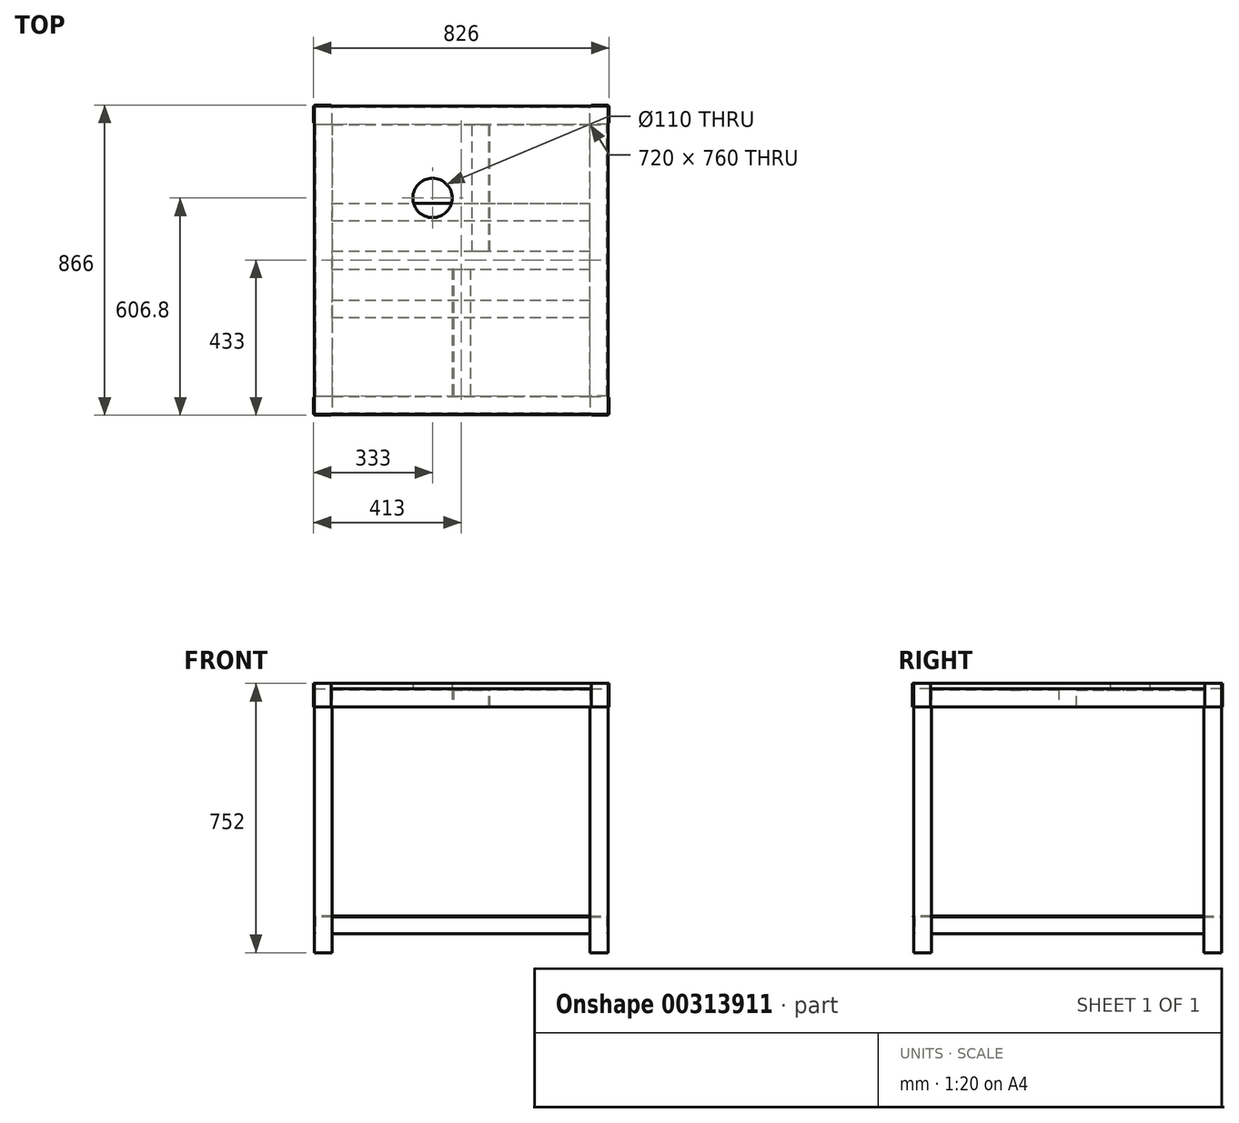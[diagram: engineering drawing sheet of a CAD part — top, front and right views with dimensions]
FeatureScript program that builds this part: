
annotation { "Feature Type Name" : "Feature", "Feature Type Description" : "" }
export const myFeature = defineFeature(function(context is Context, id is Id, definition is map)
    precondition{}
    {
        {
            var Q0;
            Q0=qCreatedBy(makeId("Top.planeOp"),FACE);
            var sketch = newSketch(context, id + "F0", { "sketchPlane" : qUnion([Q0])});
            skLineSegment(sketch, "E0", {"start": v(-475, -20) * mm, "end": v(-475, 410) * mm});
            skLineSegment(sketch, "E1", {"start": v(-475, -20) * mm, "end": v(-475, -450) * mm});
            skLineSegment(sketch, "E2", {"start": v(345, -20) * mm, "end": v(345, -450) * mm});
            skLineSegment(sketch, "E3", {"start": v(345, -20) * mm, "end": v(345, 410) * mm});
            skLineSegment(sketch, "E4", {"start": v(-425, -20) * mm, "end": v(-425, 360) * mm});
            skLineSegment(sketch, "E5", {"start": v(-425, -20) * mm, "end": v(-425, -400) * mm});
            skLineSegment(sketch, "E6", {"start": v(295, -20) * mm, "end": v(295, -400) * mm});
            skLineSegment(sketch, "E7", {"start": v(295, -20) * mm, "end": v(295, 360) * mm});
            skLineSegment(sketch, "E8", {"start": v(-425, 360) * mm, "end": v(295, 360) * mm});
            skLineSegment(sketch, "E9", {"start": v(-475, -450) * mm, "end": v(345, -450) * mm});
            skLineSegment(sketch, "E10", {"start": v(-425, -400) * mm, "end": v(295, -400) * mm});
            skLineSegment(sketch, "E11", {"start": v(-475, 410) * mm, "end": v(345, 410) * mm});
            skSolve(sketch);
        }
        {
            var Q0;
            Q0=makeQuery(id+"F0.imprint","IMPRINT",FACE,{"disambiguationData":[TD([[makeQuery(id+"F0.imprint","IMPRINT",EDGE,{"derivedFrom":sQuery(id+"F0.wireOp",EDGE,"E0")}),-1.0]])]});
            extrude(context, id + "F1", {"entities" : qUnion([Q0]), "depth" : 50 * mm});
        }
        {
            var Q0;
            Q0=makeQuery(id+"F1.opExtrude","SWEPT_BODY",BODY,{"disambiguationData":[OSD([sQuery(id+"F0.wireOp",EDGE,"E0"),sQuery(id+"F0.wireOp",EDGE,"E1"),sQuery(id+"F0.wireOp",EDGE,"E2"),sQuery(id+"F0.wireOp",EDGE,"E3"),sQuery(id+"F0.wireOp",EDGE,"E4"),sQuery(id+"F0.wireOp",EDGE,"E5"),sQuery(id+"F0.wireOp",EDGE,"E6"),sQuery(id+"F0.wireOp",EDGE,"E7"),sQuery(id+"F0.wireOp",EDGE,"E8"),sQuery(id+"F0.wireOp",EDGE,"E9"),sQuery(id+"F0.wireOp",EDGE,"E10"),sQuery(id+"F0.wireOp",EDGE,"E11")])]});
            transform(context, id + "F2", {"entities" : qUnion([Q0]), "transformType" : TransformType.TRANSLATION_3D, "dx" : 65 * mm, "dy" : 20 * mm, "dz" : 0 * mm, "makeCopy" : false});
        }
        {
            var Q0;
            Q0=makeQuery(id+"F1.opExtrude","SWEPT_BODY",BODY,{"disambiguationData":[OSD([sQuery(id+"F0.wireOp",EDGE,"E0"),sQuery(id+"F0.wireOp",EDGE,"E1"),sQuery(id+"F0.wireOp",EDGE,"E2"),sQuery(id+"F0.wireOp",EDGE,"E3"),sQuery(id+"F0.wireOp",EDGE,"E4"),sQuery(id+"F0.wireOp",EDGE,"E5"),sQuery(id+"F0.wireOp",EDGE,"E6"),sQuery(id+"F0.wireOp",EDGE,"E7"),sQuery(id+"F0.wireOp",EDGE,"E8"),sQuery(id+"F0.wireOp",EDGE,"E9"),sQuery(id+"F0.wireOp",EDGE,"E10"),sQuery(id+"F0.wireOp",EDGE,"E11")])]});
            transform(context, id + "F3", {"entities" : qUnion([Q0]), "transformType" : TransformType.TRANSLATION_3D, "dx" : 0 * mm, "dy" : 0 * mm, "dz" : -162 * mm, "makeCopy" : false});
        }
        {
            var Q0;
            Q0=qCreatedBy(makeId("Top.planeOp"),FACE);
            var sketch = newSketch(context, id + "F4", { "sketchPlane" : qUnion([Q0])});
            skLineSegment(sketch, "E12", {"start": v(-450, -20) * mm, "end": v(-450, 410) * mm});
            skLineSegment(sketch, "E13", {"start": v(370, -20) * mm, "end": v(370, -450) * mm});
            skLineSegment(sketch, "E14.bottom", {"start": v(-450, 410) * mm, "end": v(370, 410) * mm});
            skLineSegment(sketch, "E14.top", {"start": v(-450, -450) * mm, "end": v(370, -450) * mm});
            skLineSegment(sketch, "E14.left", {"start": v(-450, 410) * mm, "end": v(-450, -450) * mm});
            skLineSegment(sketch, "E14.right", {"start": v(370, 410) * mm, "end": v(370, -450) * mm});
            skSolve(sketch);
        }
        {
            var Q0;
            {var subQ0=sQuery(id+"F4.wireOp",EDGE,"E14.bottom");Q0=makeQuery(id+"F4.imprint","IMPRINT",FACE,{"disambiguationData":[TD([[makeQuery(id+"F4.imprint","IMPRINT",EDGE,{"derivedFrom":subQ0}),-1.0]])]});}
            extrude(context, id + "F5", {"entities" : qUnion([Q0]), "depth" : 15 * mm});
        }
        {
            var Q0;
            Q0=makeQuery(id+"F5.opExtrude","SWEPT_BODY",BODY,{"disambiguationData":[OSD([sQuery(id+"F4.wireOp",EDGE,"E14.bottom"),sQuery(id+"F4.wireOp",EDGE,"E14.top"),sQuery(id+"F4.wireOp",EDGE,"E14.left"),sQuery(id+"F4.wireOp",EDGE,"E14.right")])]});
            transform(context, id + "F6", {"entities" : qUnion([Q0]), "transformType" : TransformType.TRANSLATION_3D, "dx" : 0 * mm, "dy" : 0 * mm, "dz" : -112 * mm, "makeCopy" : false});
        }
        {
            var Q0;
            Q0=qCreatedBy(makeId("Top.planeOp"),FACE);
            var sketch = newSketch(context, id + "F7", { "sketchPlane" : qUnion([Q0])});
            skLineSegment(sketch, "E15", {"start": v(0, 0) * mm, "end": v(-410, 0) * mm});
            skLineSegment(sketch, "E16", {"start": v(0, 0) * mm, "end": v(410, 0) * mm});
            skLineSegment(sketch, "E17", {"start": v(-410, 0) * mm, "end": v(-410, 380) * mm});
            skLineSegment(sketch, "E18", {"start": v(410, 0) * mm, "end": v(410, 380) * mm});
            skLineSegment(sketch, "E19", {"start": v(-410, 0) * mm, "end": v(-410, -380) * mm});
            skLineSegment(sketch, "E20", {"start": v(410, 0) * mm, "end": v(410, -380) * mm});
            skLineSegment(sketch, "E21.bottom", {"start": v(-410, 380) * mm, "end": v(-360, 380) * mm});
            skLineSegment(sketch, "E21.top", {"start": v(-410, 430) * mm, "end": v(-360, 430) * mm});
            skLineSegment(sketch, "E21.left", {"start": v(-410, 380) * mm, "end": v(-410, 430) * mm});
            skLineSegment(sketch, "E21.right", {"start": v(-360, 380) * mm, "end": v(-360, 430) * mm});
            skLineSegment(sketch, "E22.bottom", {"start": v(-410, -380) * mm, "end": v(-360, -380) * mm});
            skLineSegment(sketch, "E22.top", {"start": v(-410, -430) * mm, "end": v(-360, -430) * mm});
            skLineSegment(sketch, "E22.left", {"start": v(-410, -380) * mm, "end": v(-410, -430) * mm});
            skLineSegment(sketch, "E22.right", {"start": v(-360, -380) * mm, "end": v(-360, -430) * mm});
            skLineSegment(sketch, "E23.bottom", {"start": v(410, -380) * mm, "end": v(360, -380) * mm});
            skLineSegment(sketch, "E23.top", {"start": v(410, -430) * mm, "end": v(360, -430) * mm});
            skLineSegment(sketch, "E23.left", {"start": v(410, -380) * mm, "end": v(410, -430) * mm});
            skLineSegment(sketch, "E23.right", {"start": v(360, -380) * mm, "end": v(360, -430) * mm});
            skLineSegment(sketch, "E24.bottom", {"start": v(410, 380) * mm, "end": v(360, 380) * mm});
            skLineSegment(sketch, "E24.top", {"start": v(410, 430) * mm, "end": v(360, 430) * mm});
            skLineSegment(sketch, "E24.left", {"start": v(410, 380) * mm, "end": v(410, 430) * mm});
            skLineSegment(sketch, "E24.right", {"start": v(360, 380) * mm, "end": v(360, 430) * mm});
            skLineSegment(sketch, "E25", {"start": v(-410, 0) * mm, "end": v(-410, -430) * mm});
            skLineSegment(sketch, "E26", {"start": v(-410, 0) * mm, "end": v(-410, 430) * mm});
            skSolve(sketch);
        }
        {
            var Q0;
            Q0=qSketchRegion(id+"F7",true);
            extrude(context, id + "F8", {"entities" : qUnion([Q0]), "depth" : 687 * mm});
        }
        {
            var Q0;
            Q0=makeQuery(id+"F8.opExtrude","SWEPT_BODY",BODY,{"disambiguationData":[OSD([sQuery(id+"F7.wireOp",EDGE,"E21.bottom"),sQuery(id+"F7.wireOp",EDGE,"E21.top"),sQuery(id+"F7.wireOp",EDGE,"E21.left"),sQuery(id+"F7.wireOp",EDGE,"E21.right")])]});
            var Q1;
            Q1=makeQuery(id+"F8.opExtrude","SWEPT_BODY",BODY,{"disambiguationData":[OSD([sQuery(id+"F7.wireOp",EDGE,"E22.bottom"),sQuery(id+"F7.wireOp",EDGE,"E22.top"),sQuery(id+"F7.wireOp",EDGE,"E22.left"),sQuery(id+"F7.wireOp",EDGE,"E22.right")])]});
            var Q2;
            Q2=makeQuery(id+"F8.opExtrude","SWEPT_BODY",BODY,{"disambiguationData":[OSD([sQuery(id+"F7.wireOp",EDGE,"E23.bottom"),sQuery(id+"F7.wireOp",EDGE,"E23.top"),sQuery(id+"F7.wireOp",EDGE,"E23.left"),sQuery(id+"F7.wireOp",EDGE,"E23.right")])]});
            var Q3;
            Q3=makeQuery(id+"F8.opExtrude","SWEPT_BODY",BODY,{"disambiguationData":[OSD([sQuery(id+"F7.wireOp",EDGE,"E24.bottom"),sQuery(id+"F7.wireOp",EDGE,"E24.top"),sQuery(id+"F7.wireOp",EDGE,"E24.left"),sQuery(id+"F7.wireOp",EDGE,"E24.right")])]});
            transform(context, id + "F9", {"entities" : qUnion([Q0, Q1, Q2, Q3]), "transformType" : TransformType.TRANSLATION_3D, "dx" : 0 * mm, "dy" : 0 * mm, "dz" : -849 * mm, "makeCopy" : false});
        }
        {
            var Q0;
            Q0=qCreatedBy(makeId("Top.planeOp"),FACE);
            var sketch = newSketch(context, id + "F10", { "sketchPlane" : qUnion([Q0])});
            skLineSegment(sketch, "E27", {"start": v(0, 0) * mm, "end": v(-410, 0) * mm});
            skLineSegment(sketch, "E28", {"start": v(0, 0) * mm, "end": v(410, 0) * mm});
            skLineSegment(sketch, "E29", {"start": v(-410, 0) * mm, "end": v(-410, -383) * mm});
            skLineSegment(sketch, "E30", {"start": v(410, 0) * mm, "end": v(410, -383) * mm});
            skLineSegment(sketch, "E31", {"start": v(-410, 0) * mm, "end": v(-410, 383) * mm});
            skLineSegment(sketch, "E32", {"start": v(410, 0) * mm, "end": v(410, 383) * mm});
            skLineSegment(sketch, "E33.bottom", {"start": v(-410, 383) * mm, "end": v(-413, 383) * mm});
            skLineSegment(sketch, "E33.top", {"start": v(-410, 433) * mm, "end": v(-413, 433) * mm});
            skLineSegment(sketch, "E33.left", {"start": v(-410, 383) * mm, "end": v(-410, 433) * mm});
            skLineSegment(sketch, "E33.right", {"start": v(-413, 383) * mm, "end": v(-413, 433) * mm});
            skLineSegment(sketch, "E34.bottom", {"start": v(-410, -383) * mm, "end": v(-413, -383) * mm});
            skLineSegment(sketch, "E34.top", {"start": v(-410, -433) * mm, "end": v(-413, -433) * mm});
            skLineSegment(sketch, "E34.left", {"start": v(-410, -383) * mm, "end": v(-410, -433) * mm});
            skLineSegment(sketch, "E34.right", {"start": v(-413, -383) * mm, "end": v(-413, -433) * mm});
            skLineSegment(sketch, "E35.bottom", {"start": v(410, -383) * mm, "end": v(413, -383) * mm});
            skLineSegment(sketch, "E35.top", {"start": v(410, -433) * mm, "end": v(413, -433) * mm});
            skLineSegment(sketch, "E35.left", {"start": v(410, -383) * mm, "end": v(410, -433) * mm});
            skLineSegment(sketch, "E35.right", {"start": v(413, -383) * mm, "end": v(413, -433) * mm});
            skLineSegment(sketch, "E36.bottom", {"start": v(410, 383) * mm, "end": v(413, 383) * mm});
            skLineSegment(sketch, "E36.top", {"start": v(410, 433) * mm, "end": v(413, 433) * mm});
            skLineSegment(sketch, "E36.left", {"start": v(410, 383) * mm, "end": v(410, 433) * mm});
            skLineSegment(sketch, "E36.right", {"start": v(413, 383) * mm, "end": v(413, 433) * mm});
            skLineSegment(sketch, "E37.bottom", {"start": v(-413, -433) * mm, "end": v(-363, -433) * mm});
            skLineSegment(sketch, "E37.top", {"start": v(-413, -430) * mm, "end": v(-363, -430) * mm});
            skLineSegment(sketch, "E37.left", {"start": v(-413, -433) * mm, "end": v(-413, -430) * mm});
            skLineSegment(sketch, "E37.right", {"start": v(-363, -433) * mm, "end": v(-363, -430) * mm});
            skLineSegment(sketch, "E38.bottom", {"start": v(413, -433) * mm, "end": v(363, -433) * mm});
            skLineSegment(sketch, "E38.top", {"start": v(413, -430) * mm, "end": v(363, -430) * mm});
            skLineSegment(sketch, "E38.left", {"start": v(413, -433) * mm, "end": v(413, -430) * mm});
            skLineSegment(sketch, "E38.right", {"start": v(363, -433) * mm, "end": v(363, -430) * mm});
            skLineSegment(sketch, "E39.bottom", {"start": v(-413, 433) * mm, "end": v(-363, 433) * mm});
            skLineSegment(sketch, "E39.top", {"start": v(-413, 430) * mm, "end": v(-363, 430) * mm});
            skLineSegment(sketch, "E39.left", {"start": v(-413, 433) * mm, "end": v(-413, 430) * mm});
            skLineSegment(sketch, "E39.right", {"start": v(-363, 433) * mm, "end": v(-363, 430) * mm});
            skLineSegment(sketch, "E40.bottom", {"start": v(413, 433) * mm, "end": v(363, 433) * mm});
            skLineSegment(sketch, "E40.top", {"start": v(413, 430) * mm, "end": v(363, 430) * mm});
            skLineSegment(sketch, "E40.left", {"start": v(413, 433) * mm, "end": v(413, 430) * mm});
            skLineSegment(sketch, "E40.right", {"start": v(363, 433) * mm, "end": v(363, 430) * mm});
            skSolve(sketch);
        }
        {
            var Q0;
            {var subQ0=sQuery(id+"F10.wireOp",EDGE,"E33.bottom");Q0=makeQuery(id+"F10.imprint","IMPRINT",FACE,{"disambiguationData":[TD([[makeQuery(id+"F10.imprint","IMPRINT",EDGE,{"derivedFrom":subQ0}),-1.0]])]});}
            var Q1;
            {var subQ5=sQuery(id+"F10.wireOp",EDGE,"E39.left");Q1=makeQuery(id+"F10.imprint","IMPRINT",FACE,{"disambiguationData":[TD([[makeQuery(id+"F10.imprint","IMPRINT",EDGE,{"derivedFrom":subQ5}),1.0]])]});}
            var Q2;
            {var subQ5=sQuery(id+"F10.wireOp",EDGE,"E39.right");Q2=makeQuery(id+"F10.imprint","IMPRINT",FACE,{"disambiguationData":[TD([[makeQuery(id+"F10.imprint","IMPRINT",EDGE,{"derivedFrom":subQ5}),-1.0]])]});}
            var Q3;
            {var subQ0=sQuery(id+"F10.wireOp",EDGE,"E34.bottom");Q3=makeQuery(id+"F10.imprint","IMPRINT",FACE,{"disambiguationData":[TD([[makeQuery(id+"F10.imprint","IMPRINT",EDGE,{"derivedFrom":subQ0}),1.0]])]});}
            var Q4;
            {var subQ5=sQuery(id+"F10.wireOp",EDGE,"E37.left");Q4=makeQuery(id+"F10.imprint","IMPRINT",FACE,{"disambiguationData":[TD([[makeQuery(id+"F10.imprint","IMPRINT",EDGE,{"derivedFrom":subQ5}),-1.0]])]});}
            var Q5;
            {var subQ5=sQuery(id+"F10.wireOp",EDGE,"E37.right");Q5=makeQuery(id+"F10.imprint","IMPRINT",FACE,{"disambiguationData":[TD([[makeQuery(id+"F10.imprint","IMPRINT",EDGE,{"derivedFrom":subQ5}),1.0]])]});}
            var Q6;
            {var subQ5=sQuery(id+"F10.wireOp",EDGE,"E38.right");Q6=makeQuery(id+"F10.imprint","IMPRINT",FACE,{"disambiguationData":[TD([[makeQuery(id+"F10.imprint","IMPRINT",EDGE,{"derivedFrom":subQ5}),-1.0]])]});}
            var Q7;
            {var subQ5=sQuery(id+"F10.wireOp",EDGE,"E38.left");Q7=makeQuery(id+"F10.imprint","IMPRINT",FACE,{"disambiguationData":[TD([[makeQuery(id+"F10.imprint","IMPRINT",EDGE,{"derivedFrom":subQ5}),1.0]])]});}
            var Q8;
            {var subQ0=sQuery(id+"F10.wireOp",EDGE,"E35.bottom");Q8=makeQuery(id+"F10.imprint","IMPRINT",FACE,{"disambiguationData":[TD([[makeQuery(id+"F10.imprint","IMPRINT",EDGE,{"derivedFrom":subQ0}),-1.0]])]});}
            var Q9;
            {var subQ0=sQuery(id+"F10.wireOp",EDGE,"E36.bottom");Q9=makeQuery(id+"F10.imprint","IMPRINT",FACE,{"disambiguationData":[TD([[makeQuery(id+"F10.imprint","IMPRINT",EDGE,{"derivedFrom":subQ0}),1.0]])]});}
            var Q10;
            {var subQ5=sQuery(id+"F10.wireOp",EDGE,"E40.left");Q10=makeQuery(id+"F10.imprint","IMPRINT",FACE,{"disambiguationData":[TD([[makeQuery(id+"F10.imprint","IMPRINT",EDGE,{"derivedFrom":subQ5}),-1.0]])]});}
            var Q11;
            {var subQ5=sQuery(id+"F10.wireOp",EDGE,"E40.right");Q11=makeQuery(id+"F10.imprint","IMPRINT",FACE,{"disambiguationData":[TD([[makeQuery(id+"F10.imprint","IMPRINT",EDGE,{"derivedFrom":subQ5}),1.0]])]});}
            extrude(context, id + "F11", {"entities" : qUnion([Q0, Q1, Q2, Q3, Q4, Q5, Q6, Q7, Q8, Q9, Q10, Q11]), "depth" : 65 * mm});
        }
        {
            var Q0;
            Q0=makeQuery(id+"F11.opExtrude","SWEPT_BODY",BODY,{"disambiguationData":[OSD([sQuery(id+"F10.wireOp",EDGE,"E33.bottom"),sQuery(id+"F10.wireOp",EDGE,"E33.left"),sQuery(id+"F10.wireOp",EDGE,"E33.right"),sQuery(id+"F10.wireOp",EDGE,"E39.bottom"),sQuery(id+"F10.wireOp",EDGE,"E39.top"),sQuery(id+"F10.wireOp",EDGE,"E39.left"),sQuery(id+"F10.wireOp",EDGE,"E39.right")])]});
            var Q1;
            Q1=makeQuery(id+"F11.opExtrude","SWEPT_BODY",BODY,{"disambiguationData":[OSD([sQuery(id+"F10.wireOp",EDGE,"E34.bottom"),sQuery(id+"F10.wireOp",EDGE,"E34.left"),sQuery(id+"F10.wireOp",EDGE,"E34.right"),sQuery(id+"F10.wireOp",EDGE,"E37.bottom"),sQuery(id+"F10.wireOp",EDGE,"E37.top"),sQuery(id+"F10.wireOp",EDGE,"E37.left"),sQuery(id+"F10.wireOp",EDGE,"E37.right")])]});
            var Q2;
            Q2=makeQuery(id+"F11.opExtrude","SWEPT_BODY",BODY,{"disambiguationData":[OSD([sQuery(id+"F10.wireOp",EDGE,"E35.bottom"),sQuery(id+"F10.wireOp",EDGE,"E35.left"),sQuery(id+"F10.wireOp",EDGE,"E35.right"),sQuery(id+"F10.wireOp",EDGE,"E38.bottom"),sQuery(id+"F10.wireOp",EDGE,"E38.top"),sQuery(id+"F10.wireOp",EDGE,"E38.left"),sQuery(id+"F10.wireOp",EDGE,"E38.right")])]});
            var Q3;
            Q3=makeQuery(id+"F11.opExtrude","SWEPT_BODY",BODY,{"disambiguationData":[OSD([sQuery(id+"F10.wireOp",EDGE,"E36.bottom"),sQuery(id+"F10.wireOp",EDGE,"E36.left"),sQuery(id+"F10.wireOp",EDGE,"E36.right"),sQuery(id+"F10.wireOp",EDGE,"E40.bottom"),sQuery(id+"F10.wireOp",EDGE,"E40.top"),sQuery(id+"F10.wireOp",EDGE,"E40.left"),sQuery(id+"F10.wireOp",EDGE,"E40.right")])]});
            transform(context, id + "F12", {"entities" : qUnion([Q0, Q1, Q2, Q3]), "transformType" : TransformType.TRANSLATION_3D, "dx" : 0 * mm, "dy" : 0 * mm, "dz" : -162 * mm, "makeCopy" : false});
        }
        {
            var Q0;
            Q0=qCreatedBy(makeId("Top.planeOp"),FACE);
            var sketch = newSketch(context, id + "F13", { "sketchPlane" : qUnion([Q0])});
            skLineSegment(sketch, "E41", {"start": v(0, 110) * mm, "end": v(360, 110) * mm});
            skLineSegment(sketch, "E42", {"start": v(0, 110) * mm, "end": v(-360, 110) * mm});
            skLineSegment(sketch, "E43", {"start": v(0, -160) * mm, "end": v(-360, -160) * mm});
            skLineSegment(sketch, "E44", {"start": v(0, -160) * mm, "end": v(360, -160) * mm});
            skLineSegment(sketch, "E45", {"start": v(0, -110) * mm, "end": v(-360, -110) * mm});
            skLineSegment(sketch, "E46", {"start": v(0, -110) * mm, "end": v(360, -110) * mm});
            skLineSegment(sketch, "E47", {"start": v(0, 160) * mm, "end": v(-360, 160) * mm});
            skLineSegment(sketch, "E48", {"start": v(0, 160) * mm, "end": v(360, 160) * mm});
            skLineSegment(sketch, "E49", {"start": v(-360, -160) * mm, "end": v(-360, -110) * mm});
            skLineSegment(sketch, "E50", {"start": v(-360, 110) * mm, "end": v(-360, 160) * mm});
            skLineSegment(sketch, "E51", {"start": v(360, -160) * mm, "end": v(360, -110) * mm});
            skLineSegment(sketch, "E52", {"start": v(360, 110) * mm, "end": v(360, 160) * mm});
            skSolve(sketch);
        }
        {
            var Q0;
            Q0=makeQuery(id+"F13.imprint","IMPRINT",FACE,{"disambiguationData":[TD([[makeQuery(id+"F13.imprint","IMPRINT",EDGE,{"derivedFrom":sQuery(id+"F13.wireOp",EDGE,"E43")}),-1.0]])]});
            var Q1;
            Q1=makeQuery(id+"F13.imprint","IMPRINT",FACE,{"disambiguationData":[TD([[makeQuery(id+"F13.imprint","IMPRINT",EDGE,{"derivedFrom":sQuery(id+"F13.wireOp",EDGE,"E41")}),1.0]])]});
            extrude(context, id + "F14", {"entities" : qUnion([Q0, Q1]), "depth" : 3 * mm});
        }
        {
            var Q0;
            Q0=makeQuery(id+"F14.opExtrude","SWEPT_BODY",BODY,{"disambiguationData":[OSD([sQuery(id+"F13.wireOp",EDGE,"E41"),sQuery(id+"F13.wireOp",EDGE,"E42"),sQuery(id+"F13.wireOp",EDGE,"E47"),sQuery(id+"F13.wireOp",EDGE,"E48"),sQuery(id+"F13.wireOp",EDGE,"E50"),sQuery(id+"F13.wireOp",EDGE,"E52")])]});
            var Q1;
            Q1=makeQuery(id+"F14.opExtrude","SWEPT_BODY",BODY,{"disambiguationData":[OSD([sQuery(id+"F13.wireOp",EDGE,"E43"),sQuery(id+"F13.wireOp",EDGE,"E44"),sQuery(id+"F13.wireOp",EDGE,"E45"),sQuery(id+"F13.wireOp",EDGE,"E46"),sQuery(id+"F13.wireOp",EDGE,"E49"),sQuery(id+"F13.wireOp",EDGE,"E51")])]});
            transform(context, id + "F15", {"entities" : qUnion([Q0, Q1]), "transformType" : TransformType.TRANSLATION_3D, "dx" : 0 * mm, "dy" : 0 * mm, "dz" : -115 * mm, "makeCopy" : false});
        }
        {
            var Q0;
            Q0=qCreatedBy(makeId("Top.planeOp"),FACE);
            var sketch = newSketch(context, id + "F16", { "sketchPlane" : qUnion([Q0])});
            skLineSegment(sketch, "E53", {"start": v(0, 0) * mm, "end": v(0, 157) * mm});
            skLineSegment(sketch, "E54", {"start": v(0, 0) * mm, "end": v(0, -157) * mm});
            skLineSegment(sketch, "E55", {"start": v(0, 157) * mm, "end": v(-360, 157) * mm});
            skLineSegment(sketch, "E56", {"start": v(0, 157) * mm, "end": v(360, 157) * mm});
            skLineSegment(sketch, "E57", {"start": v(0, -157) * mm, "end": v(-360, -157) * mm});
            skLineSegment(sketch, "E58", {"start": v(0, -157) * mm, "end": v(360, -157) * mm});
            skLineSegment(sketch, "E59", {"start": v(-360, 157) * mm, "end": v(-360, 160) * mm});
            skLineSegment(sketch, "E60", {"start": v(360, 157) * mm, "end": v(360, 160) * mm});
            skLineSegment(sketch, "E61", {"start": v(-360, 160) * mm, "end": v(360, 160) * mm});
            skLineSegment(sketch, "E62", {"start": v(-360, -157) * mm, "end": v(-360, -160) * mm});
            skLineSegment(sketch, "E63", {"start": v(360, -157) * mm, "end": v(360, -160) * mm});
            skLineSegment(sketch, "E64", {"start": v(-360, -160) * mm, "end": v(360, -160) * mm});
            skSolve(sketch);
        }
        {
            var Q0;
            Q0=makeQuery(id+"F16.imprint","IMPRINT",FACE,{"disambiguationData":[TD([[makeQuery(id+"F16.imprint","IMPRINT",EDGE,{"derivedFrom":sQuery(id+"F16.wireOp",EDGE,"E55")}),-1.0]])]});
            var Q1;
            Q1=makeQuery(id+"F16.imprint","IMPRINT",FACE,{"disambiguationData":[TD([[makeQuery(id+"F16.imprint","IMPRINT",EDGE,{"derivedFrom":sQuery(id+"F16.wireOp",EDGE,"E57")}),1.0]])]});
            extrude(context, id + "F17", {"entities" : qUnion([Q0, Q1]), "depth" : 50 * mm});
        }
        {
            var Q0;
            Q0=makeQuery(id+"F17.opExtrude","SWEPT_BODY",BODY,{"disambiguationData":[OSD([sQuery(id+"F16.wireOp",EDGE,"E55"),sQuery(id+"F16.wireOp",EDGE,"E56"),sQuery(id+"F16.wireOp",EDGE,"E59"),sQuery(id+"F16.wireOp",EDGE,"E60"),sQuery(id+"F16.wireOp",EDGE,"E61")])]});
            var Q1;
            Q1=makeQuery(id+"F17.opExtrude","SWEPT_BODY",BODY,{"disambiguationData":[OSD([sQuery(id+"F16.wireOp",EDGE,"E57"),sQuery(id+"F16.wireOp",EDGE,"E58"),sQuery(id+"F16.wireOp",EDGE,"E62"),sQuery(id+"F16.wireOp",EDGE,"E63"),sQuery(id+"F16.wireOp",EDGE,"E64")])]});
            transform(context, id + "F18", {"entities" : qUnion([Q0, Q1]), "transformType" : TransformType.TRANSLATION_3D, "dx" : 0 * mm, "dy" : 0 * mm, "dz" : -162 * mm, "makeCopy" : false});
        }
        {
            var Q0;
            Q0=qCreatedBy(makeId("Top.planeOp"),FACE);
            var sketch = newSketch(context, id + "F19", { "sketchPlane" : qUnion([Q0])});
            skLineSegment(sketch, "E65", {"start": v(0, 0) * mm, "end": v(0, -380) * mm});
            skLineSegment(sketch, "E66", {"start": v(0, 0) * mm, "end": v(0, 380) * mm});
            skLineSegment(sketch, "E67", {"start": v(0, 0) * mm, "end": v(-360, 0) * mm});
            skLineSegment(sketch, "E68", {"start": v(0, 0) * mm, "end": v(360, 0) * mm});
            skLineSegment(sketch, "E69", {"start": v(-360, 0) * mm, "end": v(-360, 380) * mm});
            skLineSegment(sketch, "E70", {"start": v(-360, 0) * mm, "end": v(-360, -380) * mm});
            skLineSegment(sketch, "E71", {"start": v(360, 0) * mm, "end": v(360, 380) * mm});
            skLineSegment(sketch, "E72", {"start": v(360, 0) * mm, "end": v(360, -380) * mm});
            skLineSegment(sketch, "E73", {"start": v(-360, -380) * mm, "end": v(-410, -380) * mm});
            skLineSegment(sketch, "E74", {"start": v(-360, 380) * mm, "end": v(-410, 380) * mm});
            skLineSegment(sketch, "E75", {"start": v(360, -380) * mm, "end": v(410, -380) * mm});
            skLineSegment(sketch, "E76", {"start": v(360, 380) * mm, "end": v(410, 380) * mm});
            skLineSegment(sketch, "E77", {"start": v(-410, -380) * mm, "end": v(-410, 380) * mm});
            skLineSegment(sketch, "E78", {"start": v(410, -380) * mm, "end": v(410, 380) * mm});
            skLineSegment(sketch, "E79", {"start": v(-360, -380) * mm, "end": v(-360, -430) * mm});
            skLineSegment(sketch, "E80", {"start": v(360, -380) * mm, "end": v(360, -430) * mm});
            skLineSegment(sketch, "E81", {"start": v(-360, 380) * mm, "end": v(-360, 430) * mm});
            skLineSegment(sketch, "E82", {"start": v(360, 380) * mm, "end": v(360, 430) * mm});
            skLineSegment(sketch, "E83", {"start": v(-360, -430) * mm, "end": v(360, -430) * mm});
            skLineSegment(sketch, "E84", {"start": v(-360, 430) * mm, "end": v(360, 430) * mm});
            skLineSegment(sketch, "E85", {"start": v(-360, 380) * mm, "end": v(360, 380) * mm});
            skLineSegment(sketch, "E86", {"start": v(-360, -380) * mm, "end": v(360, -380) * mm});
            skSolve(sketch);
        }
        {
            var Q0;
            {var subQ2=sQuery(id+"F19.wireOp",EDGE,"E79");Q0=makeQuery(id+"F19.imprint","IMPRINT",FACE,{"disambiguationData":[TD([[makeQuery(id+"F19.imprint","IMPRINT",EDGE,{"derivedFrom":subQ2}),1.0]])]});}
            var Q1;
            Q1=makeQuery(id+"F19.imprint","IMPRINT",FACE,{"disambiguationData":[TD([[makeQuery(id+"F19.imprint","IMPRINT",EDGE,{"derivedFrom":sQuery(id+"F19.wireOp",EDGE,"E69")}),1.0]])]});
            var Q2;
            {var subQ2=sQuery(id+"F19.wireOp",EDGE,"E81");Q2=makeQuery(id+"F19.imprint","IMPRINT",FACE,{"disambiguationData":[TD([[makeQuery(id+"F19.imprint","IMPRINT",EDGE,{"derivedFrom":subQ2}),-1.0]])]});}
            var Q3;
            Q3=makeQuery(id+"F19.imprint","IMPRINT",FACE,{"disambiguationData":[TD([[makeQuery(id+"F19.imprint","IMPRINT",EDGE,{"derivedFrom":sQuery(id+"F19.wireOp",EDGE,"E71")}),-1.0]])]});
            extrude(context, id + "F20", {"entities" : qUnion([Q0, Q1, Q2, Q3]), "depth" : 3 * mm});
        }
        {
            var Q0;
            Q0=makeQuery(id+"F20.opExtrude","SWEPT_BODY",BODY,{"disambiguationData":[OSD([sQuery(id+"F19.wireOp",EDGE,"E69"),sQuery(id+"F19.wireOp",EDGE,"E70"),sQuery(id+"F19.wireOp",EDGE,"E73"),sQuery(id+"F19.wireOp",EDGE,"E74"),sQuery(id+"F19.wireOp",EDGE,"E77")])]});
            var Q1;
            Q1=makeQuery(id+"F20.opExtrude","SWEPT_BODY",BODY,{"disambiguationData":[OSD([sQuery(id+"F19.wireOp",EDGE,"E79"),sQuery(id+"F19.wireOp",EDGE,"E80"),sQuery(id+"F19.wireOp",EDGE,"E83"),sQuery(id+"F19.wireOp",EDGE,"E86")])]});
            var Q2;
            Q2=makeQuery(id+"F20.opExtrude","SWEPT_BODY",BODY,{"disambiguationData":[OSD([sQuery(id+"F19.wireOp",EDGE,"E71"),sQuery(id+"F19.wireOp",EDGE,"E72"),sQuery(id+"F19.wireOp",EDGE,"E75"),sQuery(id+"F19.wireOp",EDGE,"E76"),sQuery(id+"F19.wireOp",EDGE,"E78")])]});
            var Q3;
            Q3=makeQuery(id+"F20.opExtrude","SWEPT_BODY",BODY,{"disambiguationData":[OSD([sQuery(id+"F19.wireOp",EDGE,"E81"),sQuery(id+"F19.wireOp",EDGE,"E82"),sQuery(id+"F19.wireOp",EDGE,"E84"),sQuery(id+"F19.wireOp",EDGE,"E85")])]});
            transform(context, id + "F21", {"entities" : qUnion([Q0, Q1, Q2, Q3]), "transformType" : TransformType.TRANSLATION_3D, "dx" : 0 * mm, "dy" : 0 * mm, "dz" : -749 * mm, "makeCopy" : false});
        }
        {
            var Q0;
            Q0=qCreatedBy(makeId("Top.planeOp"),FACE);
            var sketch = newSketch(context, id + "F22", { "sketchPlane" : qUnion([Q0])});
            skLineSegment(sketch, "E87", {"start": v(0, 0) * mm, "end": v(0, -427) * mm});
            skLineSegment(sketch, "E88", {"start": v(0, 0) * mm, "end": v(0, 427) * mm});
            skLineSegment(sketch, "E89", {"start": v(0, 0) * mm, "end": v(-407, 0) * mm});
            skLineSegment(sketch, "E90", {"start": v(0, 0) * mm, "end": v(407, 0) * mm});
            skLineSegment(sketch, "E91", {"start": v(0, 427) * mm, "end": v(-360, 427) * mm});
            skLineSegment(sketch, "E92", {"start": v(0, 427) * mm, "end": v(360, 427) * mm});
            skLineSegment(sketch, "E93", {"start": v(0, -427) * mm, "end": v(-360, -427) * mm});
            skLineSegment(sketch, "E94", {"start": v(0, -427) * mm, "end": v(360, -427) * mm});
            skLineSegment(sketch, "E95", {"start": v(-407, 0) * mm, "end": v(-407, -380) * mm});
            skLineSegment(sketch, "E96", {"start": v(-407, 0) * mm, "end": v(-407, 380) * mm});
            skLineSegment(sketch, "E97", {"start": v(407, 0) * mm, "end": v(407, 380) * mm});
            skLineSegment(sketch, "E98", {"start": v(407, 0) * mm, "end": v(407, -380) * mm});
            skLineSegment(sketch, "E99", {"start": v(-360, -427) * mm, "end": v(-360, -430) * mm});
            skLineSegment(sketch, "E100", {"start": v(-407, -380) * mm, "end": v(-410, -380) * mm});
            skLineSegment(sketch, "E101", {"start": v(360, -427) * mm, "end": v(360, -430) * mm});
            skLineSegment(sketch, "E102", {"start": v(407, -380) * mm, "end": v(410, -380) * mm});
            skLineSegment(sketch, "E103", {"start": v(407, 380) * mm, "end": v(410, 380) * mm});
            skLineSegment(sketch, "E104", {"start": v(360, 427) * mm, "end": v(360, 430) * mm});
            skLineSegment(sketch, "E105", {"start": v(-407, 380) * mm, "end": v(-410, 380) * mm});
            skLineSegment(sketch, "E106", {"start": v(-360, 427) * mm, "end": v(-360, 430) * mm});
            skLineSegment(sketch, "E107", {"start": v(-410, -380) * mm, "end": v(-410, 380) * mm});
            skLineSegment(sketch, "E108", {"start": v(-360, 430) * mm, "end": v(360, 430) * mm});
            skLineSegment(sketch, "E109", {"start": v(410, 380) * mm, "end": v(410, -380) * mm});
            skLineSegment(sketch, "E110", {"start": v(360, -430) * mm, "end": v(-360, -430) * mm});
            skSolve(sketch);
        }
        {
            var Q0;
            Q0=makeQuery(id+"F22.imprint","IMPRINT",FACE,{"disambiguationData":[TD([[makeQuery(id+"F22.imprint","IMPRINT",EDGE,{"derivedFrom":sQuery(id+"F22.wireOp",EDGE,"E93")}),1.0]])]});
            var Q1;
            Q1=makeQuery(id+"F22.imprint","IMPRINT",FACE,{"disambiguationData":[TD([[makeQuery(id+"F22.imprint","IMPRINT",EDGE,{"derivedFrom":sQuery(id+"F22.wireOp",EDGE,"E97")}),-1.0]])]});
            var Q2;
            Q2=makeQuery(id+"F22.imprint","IMPRINT",FACE,{"disambiguationData":[TD([[makeQuery(id+"F22.imprint","IMPRINT",EDGE,{"derivedFrom":sQuery(id+"F22.wireOp",EDGE,"E95")}),-1.0]])]});
            var Q3;
            Q3=makeQuery(id+"F22.imprint","IMPRINT",FACE,{"disambiguationData":[TD([[makeQuery(id+"F22.imprint","IMPRINT",EDGE,{"derivedFrom":sQuery(id+"F22.wireOp",EDGE,"E91")}),-1.0]])]});
            extrude(context, id + "F23", {"entities" : qUnion([Q0, Q1, Q2, Q3]), "depth" : 50 * mm});
        }
        {
            var Q0;
            Q0=makeQuery(id+"F23.opExtrude","SWEPT_BODY",BODY,{"disambiguationData":[OSD([sQuery(id+"F22.wireOp",EDGE,"E95"),sQuery(id+"F22.wireOp",EDGE,"E96"),sQuery(id+"F22.wireOp",EDGE,"E100"),sQuery(id+"F22.wireOp",EDGE,"E105"),sQuery(id+"F22.wireOp",EDGE,"E107")])]});
            var Q1;
            Q1=makeQuery(id+"F23.opExtrude","SWEPT_BODY",BODY,{"disambiguationData":[OSD([sQuery(id+"F22.wireOp",EDGE,"E93"),sQuery(id+"F22.wireOp",EDGE,"E94"),sQuery(id+"F22.wireOp",EDGE,"E99"),sQuery(id+"F22.wireOp",EDGE,"E101"),sQuery(id+"F22.wireOp",EDGE,"E110")])]});
            var Q2;
            Q2=makeQuery(id+"F23.opExtrude","SWEPT_BODY",BODY,{"disambiguationData":[OSD([sQuery(id+"F22.wireOp",EDGE,"E97"),sQuery(id+"F22.wireOp",EDGE,"E98"),sQuery(id+"F22.wireOp",EDGE,"E102"),sQuery(id+"F22.wireOp",EDGE,"E103"),sQuery(id+"F22.wireOp",EDGE,"E109")])]});
            var Q3;
            Q3=makeQuery(id+"F23.opExtrude","SWEPT_BODY",BODY,{"disambiguationData":[OSD([sQuery(id+"F22.wireOp",EDGE,"E91"),sQuery(id+"F22.wireOp",EDGE,"E92"),sQuery(id+"F22.wireOp",EDGE,"E104"),sQuery(id+"F22.wireOp",EDGE,"E106"),sQuery(id+"F22.wireOp",EDGE,"E108")])]});
            transform(context, id + "F24", {"entities" : qUnion([Q0, Q1, Q2, Q3]), "transformType" : TransformType.TRANSLATION_3D, "dx" : 0 * mm, "dy" : 0 * mm, "dz" : -796 * mm, "makeCopy" : false});
        }
        {
            var Q0;
            Q0=makeQuery(id+"F5.opExtrude","SWEPT_BODY",BODY,{"disambiguationData":[OSD([sQuery(id+"F4.wireOp",EDGE,"E14.bottom"),sQuery(id+"F4.wireOp",EDGE,"E14.top"),sQuery(id+"F4.wireOp",EDGE,"E14.left"),sQuery(id+"F4.wireOp",EDGE,"E14.right")])]});
            transform(context, id + "F25", {"entities" : qUnion([Q0]), "transformType" : TransformType.TRANSLATION_3D, "dx" : 40 * mm, "dy" : 20 * mm, "dz" : 0 * mm, "makeCopy" : false});
        }
        {
            var Q0;
            Q0=makeQuery(id+"F1.opExtrude","SWEPT_BODY",BODY,{"disambiguationData":[OSD([sQuery(id+"F0.wireOp",EDGE,"E0"),sQuery(id+"F0.wireOp",EDGE,"E1"),sQuery(id+"F0.wireOp",EDGE,"E2"),sQuery(id+"F0.wireOp",EDGE,"E3"),sQuery(id+"F0.wireOp",EDGE,"E4"),sQuery(id+"F0.wireOp",EDGE,"E5"),sQuery(id+"F0.wireOp",EDGE,"E6"),sQuery(id+"F0.wireOp",EDGE,"E7"),sQuery(id+"F0.wireOp",EDGE,"E8"),sQuery(id+"F0.wireOp",EDGE,"E9"),sQuery(id+"F0.wireOp",EDGE,"E10"),sQuery(id+"F0.wireOp",EDGE,"E11")])]});
            var Q1;
            Q1=makeQuery(id+"F5.opExtrude","SWEPT_BODY",BODY,{"disambiguationData":[OSD([sQuery(id+"F4.wireOp",EDGE,"E14.bottom"),sQuery(id+"F4.wireOp",EDGE,"E14.top"),sQuery(id+"F4.wireOp",EDGE,"E14.left"),sQuery(id+"F4.wireOp",EDGE,"E14.right")])]});
            var Q2;
            Q2=makeQuery(id+"F8.opExtrude","SWEPT_BODY",BODY,{"disambiguationData":[OSD([sQuery(id+"F7.wireOp",EDGE,"E22.bottom"),sQuery(id+"F7.wireOp",EDGE,"E22.top"),sQuery(id+"F7.wireOp",EDGE,"E22.right"),sQuery(id+"F7.wireOp",EDGE,"E25")])]});
            var Q3;
            Q3=makeQuery(id+"F8.opExtrude","SWEPT_BODY",BODY,{"disambiguationData":[OSD([sQuery(id+"F7.wireOp",EDGE,"E23.bottom"),sQuery(id+"F7.wireOp",EDGE,"E23.top"),sQuery(id+"F7.wireOp",EDGE,"E23.left"),sQuery(id+"F7.wireOp",EDGE,"E23.right")])]});
            var Q4;
            Q4=makeQuery(id+"F8.opExtrude","SWEPT_BODY",BODY,{"disambiguationData":[OSD([sQuery(id+"F7.wireOp",EDGE,"E24.bottom"),sQuery(id+"F7.wireOp",EDGE,"E24.top"),sQuery(id+"F7.wireOp",EDGE,"E24.left"),sQuery(id+"F7.wireOp",EDGE,"E24.right")])]});
            var Q5;
            Q5=makeQuery(id+"F11.opExtrude","SWEPT_BODY",BODY,{"disambiguationData":[OSD([sQuery(id+"F10.wireOp",EDGE,"E33.bottom"),sQuery(id+"F10.wireOp",EDGE,"E33.left"),sQuery(id+"F10.wireOp",EDGE,"E33.right"),sQuery(id+"F10.wireOp",EDGE,"E39.bottom"),sQuery(id+"F10.wireOp",EDGE,"E39.top"),sQuery(id+"F10.wireOp",EDGE,"E39.left"),sQuery(id+"F10.wireOp",EDGE,"E39.right")])]});
            var Q6;
            Q6=makeQuery(id+"F11.opExtrude","SWEPT_BODY",BODY,{"disambiguationData":[OSD([sQuery(id+"F10.wireOp",EDGE,"E34.bottom"),sQuery(id+"F10.wireOp",EDGE,"E34.left"),sQuery(id+"F10.wireOp",EDGE,"E34.right"),sQuery(id+"F10.wireOp",EDGE,"E37.bottom"),sQuery(id+"F10.wireOp",EDGE,"E37.top"),sQuery(id+"F10.wireOp",EDGE,"E37.left"),sQuery(id+"F10.wireOp",EDGE,"E37.right")])]});
            var Q7;
            Q7=makeQuery(id+"F11.opExtrude","SWEPT_BODY",BODY,{"disambiguationData":[OSD([sQuery(id+"F10.wireOp",EDGE,"E35.bottom"),sQuery(id+"F10.wireOp",EDGE,"E35.left"),sQuery(id+"F10.wireOp",EDGE,"E35.right"),sQuery(id+"F10.wireOp",EDGE,"E38.bottom"),sQuery(id+"F10.wireOp",EDGE,"E38.top"),sQuery(id+"F10.wireOp",EDGE,"E38.left"),sQuery(id+"F10.wireOp",EDGE,"E38.right")])]});
            var Q8;
            Q8=makeQuery(id+"F11.opExtrude","SWEPT_BODY",BODY,{"disambiguationData":[OSD([sQuery(id+"F10.wireOp",EDGE,"E36.bottom"),sQuery(id+"F10.wireOp",EDGE,"E36.left"),sQuery(id+"F10.wireOp",EDGE,"E36.right"),sQuery(id+"F10.wireOp",EDGE,"E40.bottom"),sQuery(id+"F10.wireOp",EDGE,"E40.top"),sQuery(id+"F10.wireOp",EDGE,"E40.left"),sQuery(id+"F10.wireOp",EDGE,"E40.right")])]});
            var Q9;
            Q9=makeQuery(id+"F23.opExtrude","SWEPT_BODY",BODY,{"disambiguationData":[OSD([sQuery(id+"F22.wireOp",EDGE,"E91"),sQuery(id+"F22.wireOp",EDGE,"E92"),sQuery(id+"F22.wireOp",EDGE,"E104"),sQuery(id+"F22.wireOp",EDGE,"E106"),sQuery(id+"F22.wireOp",EDGE,"E108")])]});
            var Q10;
            Q10=makeQuery(id+"F23.opExtrude","SWEPT_BODY",BODY,{"disambiguationData":[OSD([sQuery(id+"F22.wireOp",EDGE,"E93"),sQuery(id+"F22.wireOp",EDGE,"E94"),sQuery(id+"F22.wireOp",EDGE,"E99"),sQuery(id+"F22.wireOp",EDGE,"E101"),sQuery(id+"F22.wireOp",EDGE,"E110")])]});
            var Q11;
            Q11=makeQuery(id+"F23.opExtrude","SWEPT_BODY",BODY,{"disambiguationData":[OSD([sQuery(id+"F22.wireOp",EDGE,"E95"),sQuery(id+"F22.wireOp",EDGE,"E96"),sQuery(id+"F22.wireOp",EDGE,"E100"),sQuery(id+"F22.wireOp",EDGE,"E105"),sQuery(id+"F22.wireOp",EDGE,"E107")])]});
            var Q12;
            Q12=makeQuery(id+"F23.opExtrude","SWEPT_BODY",BODY,{"disambiguationData":[OSD([sQuery(id+"F22.wireOp",EDGE,"E97"),sQuery(id+"F22.wireOp",EDGE,"E98"),sQuery(id+"F22.wireOp",EDGE,"E102"),sQuery(id+"F22.wireOp",EDGE,"E103"),sQuery(id+"F22.wireOp",EDGE,"E109")])]});
            var Q13;
            Q13=makeQuery(id+"F8.opExtrude","SWEPT_BODY",BODY,{"disambiguationData":[OSD([sQuery(id+"F7.wireOp",EDGE,"E21.bottom"),sQuery(id+"F7.wireOp",EDGE,"E21.top"),sQuery(id+"F7.wireOp",EDGE,"E21.right"),sQuery(id+"F7.wireOp",EDGE,"E26")])]});
            var Q14;
            Q14=makeQuery(id+"F17.opExtrude","SWEPT_BODY",BODY,{"disambiguationData":[OSD([sQuery(id+"F16.wireOp",EDGE,"E55"),sQuery(id+"F16.wireOp",EDGE,"E56"),sQuery(id+"F16.wireOp",EDGE,"E59"),sQuery(id+"F16.wireOp",EDGE,"E60"),sQuery(id+"F16.wireOp",EDGE,"E61")])]});
            var Q15;
            Q15=makeQuery(id+"F17.opExtrude","SWEPT_BODY",BODY,{"disambiguationData":[OSD([sQuery(id+"F16.wireOp",EDGE,"E57"),sQuery(id+"F16.wireOp",EDGE,"E58"),sQuery(id+"F16.wireOp",EDGE,"E62"),sQuery(id+"F16.wireOp",EDGE,"E63"),sQuery(id+"F16.wireOp",EDGE,"E64")])]});
            transform(context, id + "F26", {"entities" : qUnion([Q0, Q1, Q2, Q3, Q4, Q5, Q6, Q7, Q8, Q9, Q10, Q11, Q12, Q13, Q14, Q15]), "transformType" : TransformType.TRANSLATION_3D, "dx" : 0 * mm, "dy" : 1.2 * mm, "dz" : 0 * mm, "makeCopy" : false});
        }
        {
            var Q0;
            Q0=qCreatedBy(makeId("Top.planeOp"),FACE);
            var sketch = newSketch(context, id + "F27", { "sketchPlane" : qUnion([Q0])});
            skLineSegment(sketch, "E111", {"start": v(0, 0) * mm, "end": v(0, -428.8) * mm});
            skLineSegment(sketch, "E112", {"start": v(0, 120) * mm, "end": v(0, -428.8) * mm});
            skLineSegment(sketch, "E113", {"start": v(0, 120) * mm, "end": v(-25, 120) * mm});
            skLineSegment(sketch, "E114", {"start": v(0, 120) * mm, "end": v(0, 175) * mm});
            skLineSegment(sketch, "E115", {"start": v(-25, 120) * mm, "end": v(-80, 120) * mm});
            skLineSegment(sketch, "E116", {"start": v(-80, 120) * mm, "end": v(-80, 175) * mm});
            skCircle(sketch, "E117", {"center": v(-80, 175) * mm, "radius": 55 * mm});
            skSolve(sketch);
        }
        {
            var Q0;
            Q0=makeQuery(id+"F27.imprint","IMPRINT",FACE,{"disambiguationData":[TD([[makeQuery(id+"F27.imprint","IMPRINT",EDGE,{"derivedFrom":sQuery(id+"F27.wireOp",EDGE,"E117")}),1.0]])]});
            extrude(context, id + "F28", {"entities" : qUnion([Q0]), "depth" : 25 * mm});
        }
        {
            var Q0;
            Q0=makeQuery(id+"F28.opExtrude","SWEPT_BODY",BODY,{"disambiguationData":[OSD([sQuery(id+"F27.wireOp",EDGE,"E117")])]});
            transform(context, id + "F29", {"entities" : qUnion([Q0]), "transformType" : TransformType.TRANSLATION_3D, "dx" : 0 * mm, "dy" : 0 * mm, "dz" : -120 * mm, "makeCopy" : false});
        }
        {
            var Q0;
            Q0=makeQuery(id+"F28.opExtrude","SWEPT_BODY",BODY,{"disambiguationData":[OSD([sQuery(id+"F27.wireOp",EDGE,"E117")])]});
            var Q1;
            Q1=makeQuery(id+"F5.opExtrude","SWEPT_BODY",BODY,{"disambiguationData":[OSD([sQuery(id+"F4.wireOp",EDGE,"E14.bottom"),sQuery(id+"F4.wireOp",EDGE,"E14.top"),sQuery(id+"F4.wireOp",EDGE,"E14.left"),sQuery(id+"F4.wireOp",EDGE,"E14.right")])]});
            booleanBodies(context, id + "F30", {"operationType" : BooleanOperationType.SUBTRACTION, "tools" : qUnion([Q0]), "targets" : qUnion([Q1])});
        }
        {
            var Q0;
            Q0=qCreatedBy(makeId("Top.planeOp"),FACE);
            var sketch = newSketch(context, id + "F31", { "sketchPlane" : qUnion([Q0])});
            skCircle(sketch, "E118", {"center": v(0, 0) * mm, "radius": 110 * mm});
            skSolve(sketch);
        }
        {
            var Q0;
            Q0=makeQuery(id+"F31.imprint","IMPRINT",FACE,{"disambiguationData":[TD([[makeQuery(id+"F31.imprint","IMPRINT",EDGE,{"derivedFrom":sQuery(id+"F31.wireOp",EDGE,"E118")}),1.0]])]});
            extrude(context, id + "F32", {"entities" : qUnion([Q0]), "depth" : 100 * mm});
        }
        {
            var Q0;
            Q0=makeQuery(id+"F32.opExtrude","SWEPT_BODY",BODY,{"disambiguationData":[OSD([sQuery(id+"F31.wireOp",EDGE,"E118")])]});
            transform(context, id + "F33", {"entities" : qUnion([Q0]), "transformType" : TransformType.TRANSLATION_3D, "dx" : -80 * mm, "dy" : 175 * mm, "dz" : -150 * mm, "makeCopy" : false});
        }
        {
            var Q0;
            Q0=makeQuery(id+"F17.opExtrude","SWEPT_BODY",BODY,{"disambiguationData":[OSD([sQuery(id+"F16.wireOp",EDGE,"E57"),sQuery(id+"F16.wireOp",EDGE,"E58"),sQuery(id+"F16.wireOp",EDGE,"E62"),sQuery(id+"F16.wireOp",EDGE,"E63"),sQuery(id+"F16.wireOp",EDGE,"E64")])]});
            transform(context, id + "F34", {"entities" : qUnion([Q0]), "transformType" : TransformType.TRANSLATION_3D, "dx" : 0 * mm, "dy" : 135 * mm, "dz" : 0 * mm, "makeCopy" : false});
        }
        {
            var Q0;
            Q0=qCreatedBy(makeId("Top.planeOp"),FACE);
            var sketch = newSketch(context, id + "F35", { "sketchPlane" : qUnion([Q0])});
            skLineSegment(sketch, "E119", {"start": v(0, 0) * mm, "end": v(0, -25) * mm});
            skLineSegment(sketch, "E120", {"start": v(-360, -25) * mm, "end": v(-360, 25) * mm});
            skLineSegment(sketch, "E121", {"start": v(360, -25) * mm, "end": v(360, 25) * mm});
            skLineSegment(sketch, "E122", {"start": v(-360, 25) * mm, "end": v(30, 25) * mm});
            skLineSegment(sketch, "E123", {"start": v(-360, -25) * mm, "end": v(30, -25) * mm});
            skLineSegment(sketch, "E124", {"start": v(30, -25) * mm, "end": v(360, -25) * mm});
            skLineSegment(sketch, "E125", {"start": v(30, 25) * mm, "end": v(98.81, 25) * mm});
            skLineSegment(sketch, "E126", {"start": v(98.81, 25) * mm, "end": v(360, 25) * mm});
            skSolve(sketch);
        }
        {
            var Q0;
            {var subQ2=sQuery(id+"F35.wireOp",EDGE,"E120");Q0=makeQuery(id+"F35.imprint","IMPRINT",FACE,{"disambiguationData":[TD([[makeQuery(id+"F35.imprint","IMPRINT",EDGE,{"derivedFrom":subQ2}),-1.0]])]});}
            extrude(context, id + "F36", {"entities" : qUnion([Q0]), "depth" : 50 * mm});
        }
        {
            var Q0;
            Q0=makeQuery(id+"F36.opExtrude","SWEPT_BODY",BODY,{"disambiguationData":[OSD([sQuery(id+"F35.wireOp",EDGE,"E120"),sQuery(id+"F35.wireOp",EDGE,"E121"),sQuery(id+"F35.wireOp",EDGE,"E122"),sQuery(id+"F35.wireOp",EDGE,"E123"),sQuery(id+"F35.wireOp",EDGE,"E124"),sQuery(id+"F35.wireOp",EDGE,"E125"),sQuery(id+"F35.wireOp",EDGE,"E126")])]});
            transform(context, id + "F37", {"entities" : qUnion([Q0]), "transformType" : TransformType.TRANSLATION_3D, "dx" : 0 * mm, "dy" : 1.2 * mm, "dz" : -162 * mm, "makeCopy" : false});
        }
        {
            var Q0;
            Q0=qCreatedBy(makeId("Top.planeOp"),FACE);
            var sketch = newSketch(context, id + "F38", { "sketchPlane" : qUnion([Q0])});
            skLineSegment(sketch, "E127", {"start": v(0, 0) * mm, "end": v(30, 0) * mm});
            skLineSegment(sketch, "E128", {"start": v(30, 0) * mm, "end": v(30, 25) * mm});
            skLineSegment(sketch, "E129", {"start": v(30, 25) * mm, "end": v(30, 380) * mm});
            skLineSegment(sketch, "E130", {"start": v(80, 25) * mm, "end": v(80, 380) * mm});
            skLineSegment(sketch, "E131", {"start": v(30, 380) * mm, "end": v(80, 380) * mm});
            skLineSegment(sketch, "E132", {"start": v(30, 25) * mm, "end": v(80, 25) * mm});
            skLineSegment(sketch, "E133", {"start": v(0, 0) * mm, "end": v(0, -25) * mm});
            skLineSegment(sketch, "E134", {"start": v(0, -25) * mm, "end": v(-25, -25) * mm});
            skLineSegment(sketch, "E135", {"start": v(0, -25) * mm, "end": v(25, -25) * mm});
            skLineSegment(sketch, "E136", {"start": v(-25, -25) * mm, "end": v(-25, -380) * mm});
            skLineSegment(sketch, "E137", {"start": v(25, -25) * mm, "end": v(25, -380) * mm});
            skLineSegment(sketch, "E138", {"start": v(-25, -380) * mm, "end": v(25, -380) * mm});
            skSolve(sketch);
        }
        {
            var Q0;
            Q0=makeQuery(id+"F38.imprint","IMPRINT",FACE,{"disambiguationData":[TD([[makeQuery(id+"F38.imprint","IMPRINT",EDGE,{"derivedFrom":sQuery(id+"F38.wireOp",EDGE,"E129")}),-1.0]])]});
            var Q1;
            Q1=makeQuery(id+"F38.imprint","IMPRINT",FACE,{"disambiguationData":[TD([[makeQuery(id+"F38.imprint","IMPRINT",EDGE,{"derivedFrom":sQuery(id+"F38.wireOp",EDGE,"E134")}),1.0]])]});
            extrude(context, id + "F39", {"entities" : qUnion([Q0, Q1]), "depth" : 3 * mm});
        }
        {
            var Q0;
            Q0=makeQuery(id+"F39.opExtrude","SWEPT_BODY",BODY,{"disambiguationData":[OSD([sQuery(id+"F38.wireOp",EDGE,"E129"),sQuery(id+"F38.wireOp",EDGE,"E130"),sQuery(id+"F38.wireOp",EDGE,"E131"),sQuery(id+"F38.wireOp",EDGE,"E132")])]});
            var Q1;
            Q1=makeQuery(id+"F39.opExtrude","SWEPT_BODY",BODY,{"disambiguationData":[OSD([sQuery(id+"F38.wireOp",EDGE,"E134"),sQuery(id+"F38.wireOp",EDGE,"E135"),sQuery(id+"F38.wireOp",EDGE,"E136"),sQuery(id+"F38.wireOp",EDGE,"E137"),sQuery(id+"F38.wireOp",EDGE,"E138")])]});
            transform(context, id + "F40", {"entities" : qUnion([Q0, Q1]), "transformType" : TransformType.TRANSLATION_3D, "dx" : 0 * mm, "dy" : 1.2 * mm, "dz" : -115 * mm, "makeCopy" : false});
        }
        {
            var Q0;
            Q0=makeQuery(id+"F17.opExtrude","SWEPT_BODY",BODY,{"disambiguationData":[OSD([sQuery(id+"F16.wireOp",EDGE,"E55"),sQuery(id+"F16.wireOp",EDGE,"E56"),sQuery(id+"F16.wireOp",EDGE,"E59"),sQuery(id+"F16.wireOp",EDGE,"E60"),sQuery(id+"F16.wireOp",EDGE,"E61")])]});
            deleteBodies(context, id + "F41", {"entities" : qUnion([Q0])});
        }
        {
            var Q0;
            Q0=makeQuery(id+"F17.opExtrude","SWEPT_BODY",BODY,{"disambiguationData":[OSD([sQuery(id+"F16.wireOp",EDGE,"E57"),sQuery(id+"F16.wireOp",EDGE,"E58"),sQuery(id+"F16.wireOp",EDGE,"E62"),sQuery(id+"F16.wireOp",EDGE,"E63"),sQuery(id+"F16.wireOp",EDGE,"E64")])]});
            deleteBodies(context, id + "F42", {"entities" : qUnion([Q0])});
        }
        {
            var Q0;
            Q0=makeQuery(id+"F39.opExtrude","SWEPT_BODY",BODY,{"disambiguationData":[OSD([sQuery(id+"F38.wireOp",EDGE,"E129"),sQuery(id+"F38.wireOp",EDGE,"E130"),sQuery(id+"F38.wireOp",EDGE,"E131"),sQuery(id+"F38.wireOp",EDGE,"E132")])]});
            var Q1;
            Q1=makeQuery(id+"F39.opExtrude","CAP_EDGE",EDGE,{"disambiguationData":[OSD([sQuery(id+"F38.wireOp",EDGE,"E130")])],"isStart":false});
            transform(context, id + "F43", {"entities" : qUnion([Q0]), "transformType" : TransformType.ROTATION, "transformAxis" : qUnion([Q1]), "angle" : 270 * degree, "makeCopy" : true});
        }
        {
            var Q0;
            Q0=makeQuery(id+"F43.opPattern","COPY",BODY,{"derivedFrom":makeQuery(id+"F39.opExtrude","SWEPT_BODY",BODY,{"disambiguationData":[OSD([sQuery(id+"F38.wireOp",EDGE,"E129"),sQuery(id+"F38.wireOp",EDGE,"E130"),sQuery(id+"F38.wireOp",EDGE,"E131"),sQuery(id+"F38.wireOp",EDGE,"E132")])]}),"instanceName":"1"});
            transform(context, id + "F44", {"entities" : qUnion([Q0]), "transformType" : TransformType.TRANSLATION_3D, "dx" : -3 * mm, "dy" : 0 * mm, "dz" : 0 * mm, "makeCopy" : false});
        }
        {
            var Q0;
            Q0=makeQuery(id+"F39.opExtrude","SWEPT_BODY",BODY,{"disambiguationData":[OSD([sQuery(id+"F38.wireOp",EDGE,"E134"),sQuery(id+"F38.wireOp",EDGE,"E135"),sQuery(id+"F38.wireOp",EDGE,"E136"),sQuery(id+"F38.wireOp",EDGE,"E137"),sQuery(id+"F38.wireOp",EDGE,"E138")])]});
            var Q1;
            Q1=makeQuery(id+"F39.opExtrude","CAP_EDGE",EDGE,{"disambiguationData":[OSD([sQuery(id+"F38.wireOp",EDGE,"E136")])],"isStart":false});
            transform(context, id + "F45", {"entities" : qUnion([Q0]), "transformType" : TransformType.ROTATION, "transformAxis" : qUnion([Q1]), "angle" : 270 * degree, "makeCopy" : true});
        }
        {
            var Q0;
            Q0=makeQuery(id+"F45.opPattern","COPY",BODY,{"derivedFrom":makeQuery(id+"F39.opExtrude","SWEPT_BODY",BODY,{"disambiguationData":[OSD([sQuery(id+"F38.wireOp",EDGE,"E134"),sQuery(id+"F38.wireOp",EDGE,"E135"),sQuery(id+"F38.wireOp",EDGE,"E136"),sQuery(id+"F38.wireOp",EDGE,"E137"),sQuery(id+"F38.wireOp",EDGE,"E138")])]}),"instanceName":"1"});
            transform(context, id + "F46", {"entities" : qUnion([Q0]), "transformType" : TransformType.TRANSLATION_3D, "dx" : 3 * mm, "dy" : 0 * mm, "dz" : 0 * mm, "makeCopy" : false});
        }
        {
            var Q0;
            Q0=makeQuery(id+"F32.opExtrude","SWEPT_BODY",BODY,{"disambiguationData":[OSD([sQuery(id+"F31.wireOp",EDGE,"E118")])]});
            deleteBodies(context, id + "F47", {"entities" : qUnion([Q0])});
        }
    });
